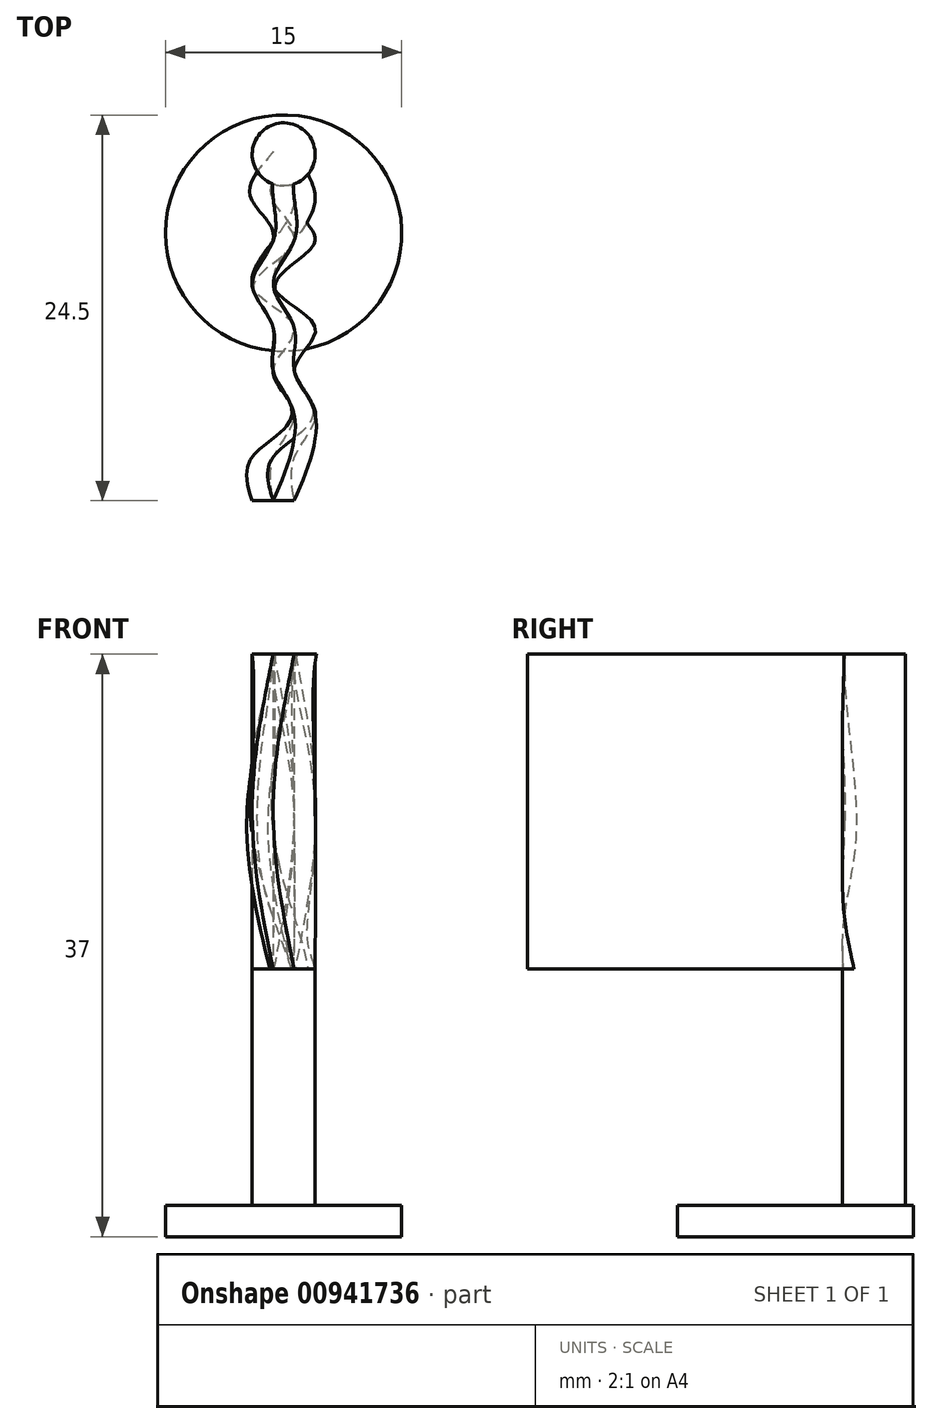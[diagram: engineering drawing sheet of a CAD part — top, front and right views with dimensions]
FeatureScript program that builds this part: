
annotation { "Feature Type Name" : "Feature", "Feature Type Description" : "" }
export const myFeature = defineFeature(function(context is Context, id is Id, definition is map)
    precondition{}
    {
        {
            var Q0;
            Q0=qCreatedBy(makeId("Top.planeOp"),FACE);
            var sketch = newSketch(context, id + "F0", { "sketchPlane" : qUnion([Q0])});
            skCircle(sketch, "E0", {"center": v(0, 0) * mm, "radius": 7.5 * mm});
            skSolve(sketch);
        }
        {
            var Q0;
            Q0=makeQuery(id+"F0.imprint","IMPRINT",FACE,{"disambiguationData":[TD([[makeQuery(id+"F0.imprint","IMPRINT",EDGE,{"derivedFrom":sQuery(id+"F0.wireOp",EDGE,"E0")}),1.0]])]});
            extrude(context, id + "F1", {"entities" : qUnion([Q0]), "depth" : 2 * mm, "offsetDistance" : 25 * mm});
        }
        {
            var Q0;
            Q0=makeQuery(id+"F1.opExtrude","CAP_FACE",FACE,{"disambiguationData":[OSD([sQuery(id+"F0.wireOp",EDGE,"E0")])],"isStart":false});
            var sketch = newSketch(context, id + "F2", { "sketchPlane" : qUnion([Q0])});
            skCircle(sketch, "E1", {"center": v(0, 0) * mm, "radius": 2 * mm});
            skSolve(sketch);
        }
        {
            var Q0;
            Q0=makeQuery(id+"F2.imprint","IMPRINT",FACE,{"disambiguationData":[TD([[makeQuery(id+"F2.imprint","IMPRINT",EDGE,{"derivedFrom":sQuery(id+"F2.wireOp",EDGE,"E1")}),1.0]])]});
            extrude(context, id + "F3", {"entities" : qUnion([Q0]), "operationType" : NewBodyOperationType.ADD, "depth" : 35 * mm, "offsetDistance" : 25 * mm});
        }
        {
            var Q0;
            Q0=makeQuery(id+"F1.opExtrude","CAP_FACE",FACE,{"disambiguationData":[OSD([sQuery(id+"F0.wireOp",EDGE,"E0")])],"isStart":false});
            cPlane(context, id + "F4", {"entities" : qUnion([Q0]), "cplaneType" : CPlaneType.OFFSET, "offset" : 15 * mm, "width" : 150 * mm, "height" : 150 * mm});
        }
        {
            var Q0;
            Q0=qCreatedBy(id+"F4.planeOp",FACE);
            cPlane(context, id + "F5", {"entities" : qUnion([Q0]), "cplaneType" : CPlaneType.OFFSET, "offset" : 10 * mm, "width" : 150 * mm, "height" : 150 * mm});
        }
        {
            var Q0;
            Q0=qCreatedBy(id+"F4.planeOp",FACE);
            var sketch = newSketch(context, id + "F6", { "sketchPlane" : qUnion([Q0])});
            skCircle(sketch, "E2.0.0", {"center": v(0, 0) * mm, "radius": 2 * mm, "construction": true});
            skLineSegment(sketch, "E3", {"start": v(0, 0) * mm, "end": v(2, 0) * mm, "construction": true});
            skLineSegment(sketch, "E4", {"start": v(0, 0) * mm, "end": v(-2, 0) * mm, "construction": true});
            skLineSegment(sketch, "E5", {"start": v(-2, 0) * mm, "end": v(-2, -22) * mm, "construction": true});
            skLineSegment(sketch, "E6", {"start": v(-2, -22) * mm, "end": v(2, -22) * mm, "construction": true});
            skLineSegment(sketch, "E7", {"start": v(2, -22) * mm, "end": v(2, 0) * mm, "construction": true});
            skLineSegment(sketch, "E8", {"start": v(0.67, -22) * mm, "end": v(0.67, 0) * mm, "construction": true});
            skLineSegment(sketch, "E9", {"start": v(-2, -11) * mm, "end": v(-0.67, -11) * mm, "construction": true});
            skLineSegment(sketch, "E10", {"start": v(-0.67, -11) * mm, "end": v(0.67, -11) * mm, "construction": true});
            skLineSegment(sketch, "E11", {"start": v(0.67, -11) * mm, "end": v(2, -11) * mm, "construction": true});
            skPoint(sketch, "E12", {"position": v(-2, -5.5) * mm});
            skPoint(sketch, "E13", {"position": v(-0.67, -5.5) * mm});
            skPoint(sketch, "E14", {"position": v(0.67, -5.5) * mm});
            skPoint(sketch, "E15", {"position": v(2, -5.5) * mm});
            skPoint(sketch, "E16", {"position": v(-2, -16.5) * mm});
            skPoint(sketch, "E17", {"position": v(-0.67, -16.5) * mm});
            skPoint(sketch, "E18", {"position": v(0.67, -16.5) * mm});
            skPoint(sketch, "E19", {"position": v(2, -16.5) * mm});
            skPoint(sketch, "E20", {"position": v(-2, -13.75) * mm});
            skPoint(sketch, "E21", {"position": v(-0.67, -13.75) * mm});
            skPoint(sketch, "E22", {"position": v(0.67, -13.75) * mm});
            skPoint(sketch, "E23", {"position": v(2, -13.75) * mm});
            skPoint(sketch, "E24", {"position": v(2, -19.25) * mm});
            skPoint(sketch, "E25", {"position": v(0.67, -19.25) * mm});
            skPoint(sketch, "E26", {"position": v(-0.67, -19.25) * mm});
            skPoint(sketch, "E27", {"position": v(-2, -19.25) * mm});
            skPoint(sketch, "E28", {"position": v(-2, -8.25) * mm});
            skPoint(sketch, "E29", {"position": v(-0.67, -8.25) * mm});
            skPoint(sketch, "E30", {"position": v(0.67, -8.25) * mm});
            skPoint(sketch, "E31", {"position": v(2, -8.25) * mm});
            skPoint(sketch, "E32", {"position": v(2, -2.75) * mm});
            skPoint(sketch, "E33", {"position": v(0.67, -2.75) * mm});
            skPoint(sketch, "E34", {"position": v(-0.67, -2.75) * mm});
            skPoint(sketch, "E35", {"position": v(-2, -2.75) * mm});
            skLineSegment(sketch, "E36", {"start": v(-0.67, -19.25) * mm, "end": v(-0.67, -16.5) * mm, "construction": true});
            skLineSegment(sketch, "E37", {"start": v(-0.67, -19.25) * mm, "end": v(-0.67, -22) * mm, "construction": true});
            skLineSegment(sketch, "E38", {"start": v(-0.67, -16.5) * mm, "end": v(-0.67, -13.75) * mm, "construction": true});
            skLineSegment(sketch, "E39", {"start": v(-0.67, -11) * mm, "end": v(-0.67, -8.25) * mm, "construction": true});
            skLineSegment(sketch, "E40", {"start": v(-0.67, -5.5) * mm, "end": v(-0.67, -2.75) * mm, "construction": true});
            skLineSegment(sketch, "E41", {"start": v(-0.67, -2.75) * mm, "end": v(-0.67, 0) * mm, "construction": true});
            skLineSegment(sketch, "E42", {"start": v(-0.67, -5.5) * mm, "end": v(-0.67, -8.25) * mm, "construction": true});
            skLineSegment(sketch, "E43", {"start": v(-0.67, -11) * mm, "end": v(-0.67, -13.75) * mm, "construction": true});
            skFitSpline(sketch, "E44", {"points": [v(-0.67, 0) * mm, v(0.67, -2.75) * mm, v(-0.67, -5.5) * mm, v(-2, -8.25) * mm, v(-0.67, -11) * mm, v(-0.67, -13.75) * mm, v(0.67, -16.5) * mm, v(-0.67, -19.25) * mm, v(-0.67, -22) * mm], "startDerivative": vector(15.66, -20.02) * mm, "endDerivative": vector(4.49, -21.57) * mm});
            skFitSpline(sketch, "E45", {"points": [v(0.67, 0) * mm, v(2, -2.75) * mm, v(0.67, -5.5) * mm, v(-0.67, -8.25) * mm, v(0.67, -11) * mm, v(0.67, -13.75) * mm, v(2, -16.5) * mm, v(0.67, -19.25) * mm, v(0.67, -22) * mm], "startDerivative": vector(15.66, -20.02) * mm, "endDerivative": vector(4.49, -21.57) * mm});
            skLineSegment(sketch, "E46", {"start": v(-0.67, -22) * mm, "end": v(0.67, -22) * mm});
            skLineSegment(sketch, "E47", {"start": v(-0.67, 0) * mm, "end": v(0.67, 0) * mm});
            skSolve(sketch);
        }
        {
            var Q0;
            Q0=qCreatedBy(id+"F5.planeOp",FACE);
            var sketch = newSketch(context, id + "F7", { "sketchPlane" : qUnion([Q0])});
            skLineSegment(sketch, "E48.0", {"start": v(2, -22) * mm, "end": v(2, 0) * mm, "construction": true});
            skLineSegment(sketch, "E49.0", {"start": v(-0.67, -5.5) * mm, "end": v(-0.67, -2.75) * mm, "construction": true});
            skLineSegment(sketch, "E49.1", {"start": v(-0.67, -11) * mm, "end": v(-0.67, -8.25) * mm, "construction": true});
            skLineSegment(sketch, "E49.2", {"start": v(-2, -22) * mm, "end": v(2, -22) * mm, "construction": true});
            skLineSegment(sketch, "E49.3", {"start": v(-0.67, -2.75) * mm, "end": v(-0.67, 0) * mm, "construction": true});
            skLineSegment(sketch, "E49.5", {"start": v(-2, 0) * mm, "end": v(-2, -22) * mm, "construction": true});
            skLineSegment(sketch, "E49.6", {"start": v(0.67, -11) * mm, "end": v(2, -11) * mm, "construction": true});
            skLineSegment(sketch, "E49.7", {"start": v(-2, -11) * mm, "end": v(-0.67, -11) * mm, "construction": true});
            skLineSegment(sketch, "E49.8", {"start": v(-0.67, -16.5) * mm, "end": v(-0.67, -13.75) * mm, "construction": true});
            skLineSegment(sketch, "E49.9", {"start": v(-0.67, -5.5) * mm, "end": v(-0.67, -8.25) * mm, "construction": true});
            skLineSegment(sketch, "E49.10", {"start": v(-0.67, -19.25) * mm, "end": v(-0.67, -16.5) * mm, "construction": true});
            skFitSpline(sketch, "E49.11", {"points": [v(-0.67, 0) * mm, v(0, -0.85) * mm, v(1.32, -2.54) * mm, v(-0.61, -5.07) * mm, v(-2.87, -7.63) * mm, v(0.03, -10.05) * mm, v(-1.4, -12.8) * mm, v(1.68, -15.23) * mm, v(-1.21, -17.68) * mm, v(-0.85, -19.45) * mm, v(-0.67, -20.31) * mm], "construction": true});
            skLineSegment(sketch, "E49.12", {"start": v(-0.67, -19.25) * mm, "end": v(-0.67, -22) * mm, "construction": true});
            skLineSegment(sketch, "E49.13", {"start": v(-0.67, -11) * mm, "end": v(-0.67, -13.75) * mm, "construction": true});
            skLineSegment(sketch, "E50.0", {"start": v(0.67, -22) * mm, "end": v(0.67, 0) * mm, "construction": true});
            skLineSegment(sketch, "E51.0", {"start": v(-0.67, -11) * mm, "end": v(0.67, -11) * mm, "construction": true});
            skPoint(sketch, "E52.0", {"position": v(-2, -13.75) * mm});
            skPoint(sketch, "E53.0", {"position": v(-2, -16.5) * mm});
            skPoint(sketch, "E54.0", {"position": v(-2, -19.25) * mm});
            skPoint(sketch, "E55.0", {"position": v(0.67, -19.25) * mm});
            skPoint(sketch, "E56.0", {"position": v(0.67, -16.5) * mm});
            skPoint(sketch, "E57.0", {"position": v(0.67, -13.75) * mm});
            skPoint(sketch, "E58.0", {"position": v(2, -13.75) * mm});
            skPoint(sketch, "E59.0", {"position": v(2, -16.5) * mm});
            skPoint(sketch, "E60.0", {"position": v(2, -19.25) * mm});
            skPoint(sketch, "E61.0", {"position": v(-2, -8.25) * mm});
            skPoint(sketch, "E62.0", {"position": v(-0.67, -8.25) * mm});
            skPoint(sketch, "E63.0", {"position": v(0.67, -8.25) * mm});
            skPoint(sketch, "E64.0", {"position": v(2, -8.25) * mm});
            skPoint(sketch, "E65.0", {"position": v(2, -5.5) * mm});
            skPoint(sketch, "E66.0", {"position": v(0.67, -5.5) * mm});
            skPoint(sketch, "E67.0", {"position": v(-0.67, -5.5) * mm});
            skPoint(sketch, "E68.0", {"position": v(-2, -5.5) * mm});
            skPoint(sketch, "E69.0", {"position": v(-2, -2.75) * mm});
            skPoint(sketch, "E70.0", {"position": v(-0.67, -2.75) * mm});
            skPoint(sketch, "E71.0", {"position": v(0.67, -2.75) * mm});
            skPoint(sketch, "E72.0", {"position": v(2, -2.75) * mm});
            skLineSegment(sketch, "E73", {"start": v(-0.67, 0) * mm, "end": v(0.67, 0) * mm});
            skLineSegment(sketch, "E74", {"start": v(-0.67, -22) * mm, "end": v(0.67, -22) * mm});
            skFitSpline(sketch, "E75", {"points": [v(-0.67, 0) * mm, v(-2, -2.75) * mm, v(0.67, -5.5) * mm, v(-2, -8.25) * mm, v(0.67, -11) * mm, v(-0.67, -13.75) * mm, v(0.67, -16.5) * mm, v(-2, -19.25) * mm, v(-2, -22) * mm], "startDerivative": vector(-22.8, -22.16) * mm, "endDerivative": vector(7.71, -23.98) * mm});
            skFitSpline(sketch, "E76", {"points": [v(0.67, 0) * mm, v(-0.67, -2.75) * mm, v(2, -5.5) * mm, v(-0.67, -8.25) * mm, v(2, -11) * mm, v(0.67, -13.75) * mm, v(2, -16.5) * mm, v(-0.67, -19.25) * mm, v(-0.67, -22) * mm], "startDerivative": vector(-22.8, -22.16) * mm, "endDerivative": vector(7.71, -23.98) * mm});
            skLineSegment(sketch, "E77", {"start": v(-0.67, -22) * mm, "end": v(-2, -22) * mm});
            skSolve(sketch);
        }
        {
            var Q0;
            Q0=makeQuery(id+"F3.opExtrude","CAP_FACE",FACE,{"disambiguationData":[OSD([sQuery(id+"F2.wireOp",EDGE,"E1")])],"isStart":false});
            var sketch = newSketch(context, id + "F8", { "sketchPlane" : qUnion([Q0])});
            skLineSegment(sketch, "E78.0", {"start": v(0.67, -22) * mm, "end": v(0.67, 0) * mm, "construction": true});
            skLineSegment(sketch, "E78.1", {"start": v(-0.67, -11) * mm, "end": v(-0.67, -8.25) * mm, "construction": true});
            skLineSegment(sketch, "E78.2", {"start": v(0, 0) * mm, "end": v(2, 0) * mm, "construction": true});
            skCircle(sketch, "E78.3", {"center": v(0, 0) * mm, "radius": 2 * mm, "construction": true});
            skLineSegment(sketch, "E78.4", {"start": v(-2, -22) * mm, "end": v(2, -22) * mm, "construction": true});
            skLineSegment(sketch, "E78.5", {"start": v(-0.67, -22) * mm, "end": v(0.67, -22) * mm, "construction": true});
            skLineSegment(sketch, "E78.6", {"start": v(-2, 0) * mm, "end": v(-2, -22) * mm, "construction": true});
            skLineSegment(sketch, "E78.7", {"start": v(0.67, -11) * mm, "end": v(2, -11) * mm, "construction": true});
            skLineSegment(sketch, "E78.8", {"start": v(-2, -11) * mm, "end": v(-0.67, -11) * mm, "construction": true});
            skLineSegment(sketch, "E78.9", {"start": v(2, -22) * mm, "end": v(2, 0) * mm, "construction": true});
            skLineSegment(sketch, "E78.10", {"start": v(-0.67, -11) * mm, "end": v(0.67, -11) * mm, "construction": true});
            skLineSegment(sketch, "E78.11", {"start": v(0, 0) * mm, "end": v(-2, 0) * mm, "construction": true});
            skLineSegment(sketch, "E78.14", {"start": v(-0.67, -19.25) * mm, "end": v(-0.67, -22) * mm, "construction": true});
            skLineSegment(sketch, "E78.16", {"start": v(2, -22) * mm, "end": v(2, 0) * mm, "construction": true});
            skLineSegment(sketch, "E78.17", {"start": v(-0.67, -2.75) * mm, "end": v(-0.67, 0) * mm, "construction": true});
            skLineSegment(sketch, "E78.18", {"start": v(-2, -11) * mm, "end": v(-0.67, -11) * mm, "construction": true});
            skLineSegment(sketch, "E78.20", {"start": v(-2, 0) * mm, "end": v(-2, -22) * mm, "construction": true});
            skLineSegment(sketch, "E78.21", {"start": v(-0.67, -20.31) * mm, "end": v(0.67, -20.31) * mm, "construction": true});
            skLineSegment(sketch, "E78.23", {"start": v(-0.67, -16.5) * mm, "end": v(-0.67, -13.75) * mm, "construction": true});
            skLineSegment(sketch, "E78.24", {"start": v(0.67, -22) * mm, "end": v(0.67, 0) * mm, "construction": true});
            skLineSegment(sketch, "E78.25", {"start": v(-2, -22) * mm, "end": v(2, -22) * mm, "construction": true});
            skLineSegment(sketch, "E78.26", {"start": v(-0.67, 0) * mm, "end": v(0.67, 0) * mm, "construction": true});
            skLineSegment(sketch, "E78.27", {"start": v(0.67, -11) * mm, "end": v(2, -11) * mm, "construction": true});
            skLineSegment(sketch, "E78.28", {"start": v(-0.67, -11) * mm, "end": v(0.67, -11) * mm, "construction": true});
            skCircle(sketch, "E78.31", {"center": v(0, 0) * mm, "radius": 2 * mm, "construction": true});
            skLineSegment(sketch, "E78.32", {"start": v(-0.67, -5.5) * mm, "end": v(-0.67, -2.75) * mm, "construction": true});
            skLineSegment(sketch, "E78.33", {"start": v(-0.67, -11) * mm, "end": v(-0.67, -13.75) * mm, "construction": true});
            skLineSegment(sketch, "E78.34", {"start": v(-0.67, -5.5) * mm, "end": v(-0.67, -8.25) * mm, "construction": true});
            skLineSegment(sketch, "E78.35", {"start": v(-0.67, -19.25) * mm, "end": v(-0.67, -16.5) * mm, "construction": true});
            skLineSegment(sketch, "E78.36", {"start": v(-0.67, 0) * mm, "end": v(0.67, 0) * mm, "construction": true});
            skLineSegment(sketch, "E78.37", {"start": v(-0.67, -5.5) * mm, "end": v(-0.67, -8.25) * mm, "construction": true});
            skLineSegment(sketch, "E78.38", {"start": v(-0.67, -2.75) * mm, "end": v(-0.67, 0) * mm, "construction": true});
            skLineSegment(sketch, "E78.39", {"start": v(-0.67, -2.75) * mm, "end": v(-0.67, 0) * mm, "construction": true});
            skFitSpline(sketch, "E79", {"points": [v(-0.67, 0) * mm, v(-0.67, -2.75) * mm, v(-0.67, -5.5) * mm, v(-2, -8.25) * mm, v(-0.67, -11) * mm, v(-0.67, -13.75) * mm, v(0.67, -16.5) * mm, v(-0.67, -22) * mm], "startDerivative": vector(-1.1, -19.3) * mm, "endDerivative": vector(-13.3, -29.71) * mm});
            skFitSpline(sketch, "E80", {"points": [v(0.67, 0) * mm, v(0.67, -2.75) * mm, v(0.67, -5.5) * mm, v(-0.67, -8.25) * mm, v(0.67, -11) * mm, v(0.67, -13.75) * mm, v(2, -16.5) * mm, v(0.67, -22) * mm], "startDerivative": vector(-1.1, -19.3) * mm, "endDerivative": vector(-13.3, -29.71) * mm});
            skLineSegment(sketch, "E81", {"start": v(-0.67, -22) * mm, "end": v(0.67, -22) * mm});
            skLineSegment(sketch, "E82", {"start": v(-0.67, 0) * mm, "end": v(0.67, 0) * mm});
            skSolve(sketch);
        }
        {
            var Q1;
            Q1 = qSketchRegion(id + "F6", true);
            var Q2;
            Q2 = qSketchRegion(id + "F7", true);
            var Q3;
            {var subQ0=sQuery(id+"F8.wireOp",EDGE,"E81");Q3=makeQuery(id+"F8.imprint","IMPRINT",FACE,{"disambiguationData":[TD([[makeQuery(id+"F8.imprint","IMPRINT",EDGE,{"derivedFrom":subQ0}),1.0]])]});}
            loft(context, id + "F9", {"operationType" : NewBodyOperationType.ADD, "sheetProfilesArray" : [{ "sheetProfileEntities" : qUnion([Q1]) }, { "sheetProfileEntities" : qUnion([Q2]) }, { "sheetProfileEntities" : qUnion([Q3]) }]});
        }
        {
            var Q0;
            Q0=makeQuery(id+"F1.opExtrude","CAP_FACE",FACE,{"disambiguationData":[OSD([sQuery(id+"F0.wireOp",EDGE,"E0")])],"isStart":true});
            var Q1;
            Q1=makeQuery(id+"F1.opExtrude","CAP_FACE",FACE,{"disambiguationData":[OSD([sQuery(id+"F0.wireOp",EDGE,"E0")])],"isStart":false});
            extrude(context, id + "F10", {"entities" : qUnion([Q0]), "operationType" : NewBodyOperationType.REMOVE, "endBound" : BoundingType.UP_TO_SURFACE, "oppositeDirection" : true, "depth" : 25 * mm, "endBoundEntityFace" : qUnion([Q1]), "offsetDistance" : 25 * mm});
        }
        {
            var Q0;
            Q0=makeQuery(id+"F10.boolean.opBoolean","COPY",FACE,{"derivedFrom":makeQuery(id+"F10.opExtrude","CAP_FACE",FACE,{"disambiguationData":[OSD([sQuery(id+"F0.wireOp",EDGE,"E0")])],"isStart":false})});
            var sketch = newSketch(context, id + "F11", { "sketchPlane" : qUnion([Q0])});
            skCircle(sketch, "E83", {"center": v(0, 5) * mm, "radius": 7.5 * mm});
            skLineSegment(sketch, "E84", {"start": v(0, 5) * mm, "end": v(0, 0) * mm, "construction": true});
            skLineSegment(sketch, "E85", {"start": v(0, 0) * mm, "end": v(0, -2.5) * mm, "construction": true});
            skSolve(sketch);
        }
        {
            var Q0;
            Q0 = qSketchRegion(id + "F11", true);
            extrude(context, id + "F12", {"entities" : qUnion([Q0]), "operationType" : NewBodyOperationType.ADD, "depth" : 2 * mm, "offsetDistance" : 25 * mm});
        }
    });
